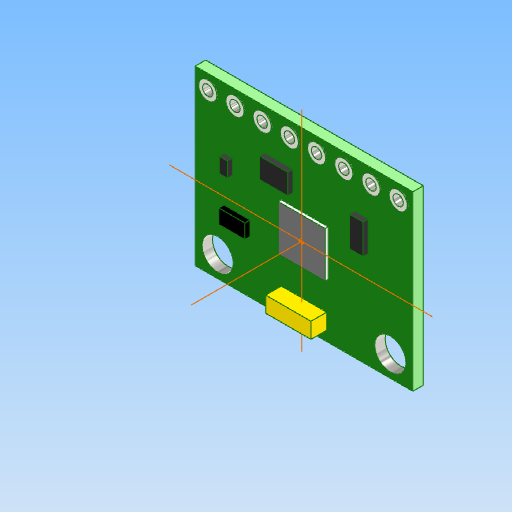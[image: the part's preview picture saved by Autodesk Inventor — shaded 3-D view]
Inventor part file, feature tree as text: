
AUTODESK INVENTOR PART (.ipt)
format: ipt  version: 2021.2 (Build 252289000, 289)  size: 222,720 bytes
history: native  units: mm
features: extrude x6, other x5, sketch x3, pattern_linear x1, projected_geometry x1
ambient origin geometry x8: Origin, YZ Plane, XZ Plane, XY Plane, X Axis, Y Axis, Z Axis, Center Point
bodies: Body1 (feature_tree)
feature tree (16):
  other  "Твердое тело1"
  sketch  "Эскиз1"
  extrude  "Выдавливание1"  Depth=20.8mm
  extrude  "Выдавливание2"  Depth=16.5mm
  extrude  "Выдавливание3"  Depth=3.0mm
  pattern_linear  "Прямоуг.массив1"  Spacing1=3.0mm  [1 undecoded]
  sketch  "Эскиз2"
  extrude  "Выдавливание4"  Depth=13.5mm
  extrude  "Выдавливание5"  Depth=0.5mm
  extrude  "Выдавливание6"  Depth=2.15mm
  sketch  "Эскиз3"
  other  "РабТочка1"
  other  "РабОсь1"
  other  "РабОсь2"
  other  "РабОсь3"
  projected_geometry  "Спроецированная петля1"
note: 1 required parameter value undecoded (feature->parameter linkage not recoverable at this tier; creation-order binding heuristic only, values carry confidence <= 0.55)
